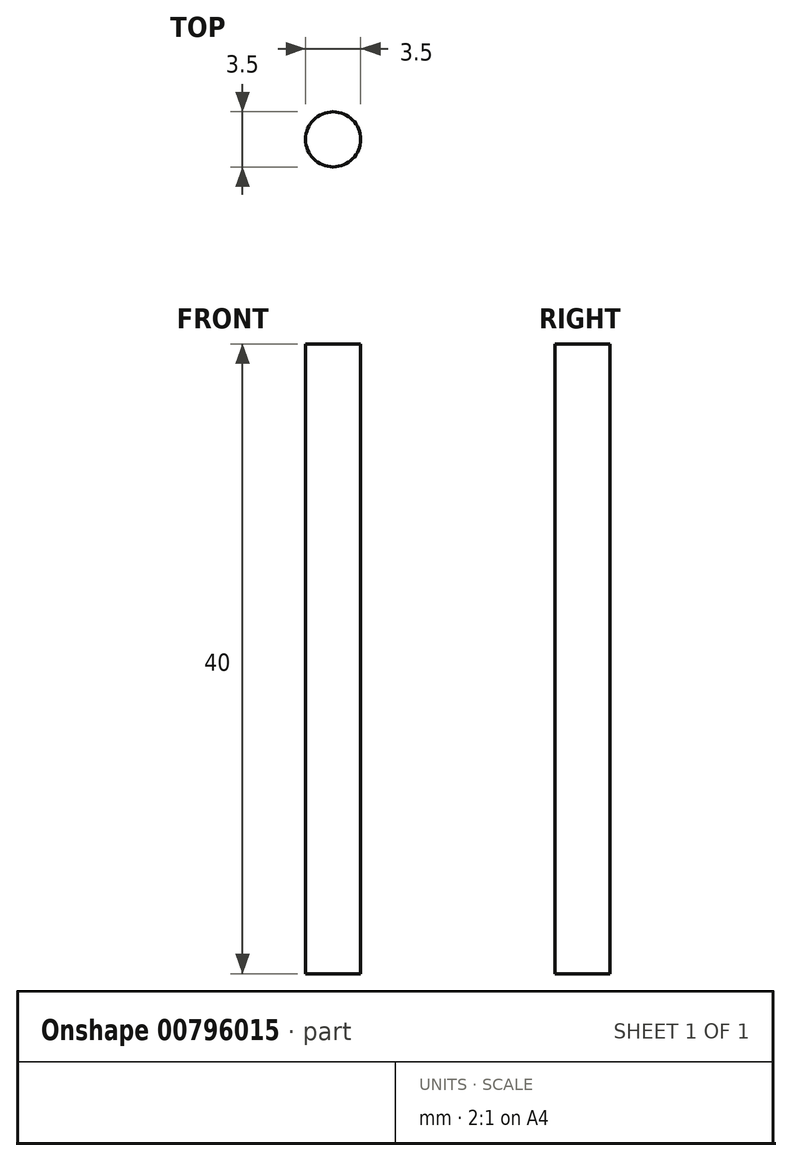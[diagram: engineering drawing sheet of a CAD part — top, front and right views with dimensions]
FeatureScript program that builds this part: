
annotation { "Feature Type Name" : "Feature", "Feature Type Description" : "" }
export const myFeature = defineFeature(function(context is Context, id is Id, definition is map)
    precondition{}
    {
        {
            var Q0;
            Q0=qCreatedBy(makeId("Top.planeOp"),FACE);
            var sketch = newSketch(context, id + "F0", { "sketchPlane" : qUnion([Q0])});
            skCircle(sketch, "E0", {"center": v(0, 0) * mm, "radius": 1.75 * mm});
            skSolve(sketch);
        }
        {
            var Q0;
            Q0 = qSketchRegion(id + "F0", true);
            extrude(context, id + "F1", {"entities" : qUnion([Q0]), "depth" : 40 * mm, "offsetDistance" : 25 * mm});
        }
    });
